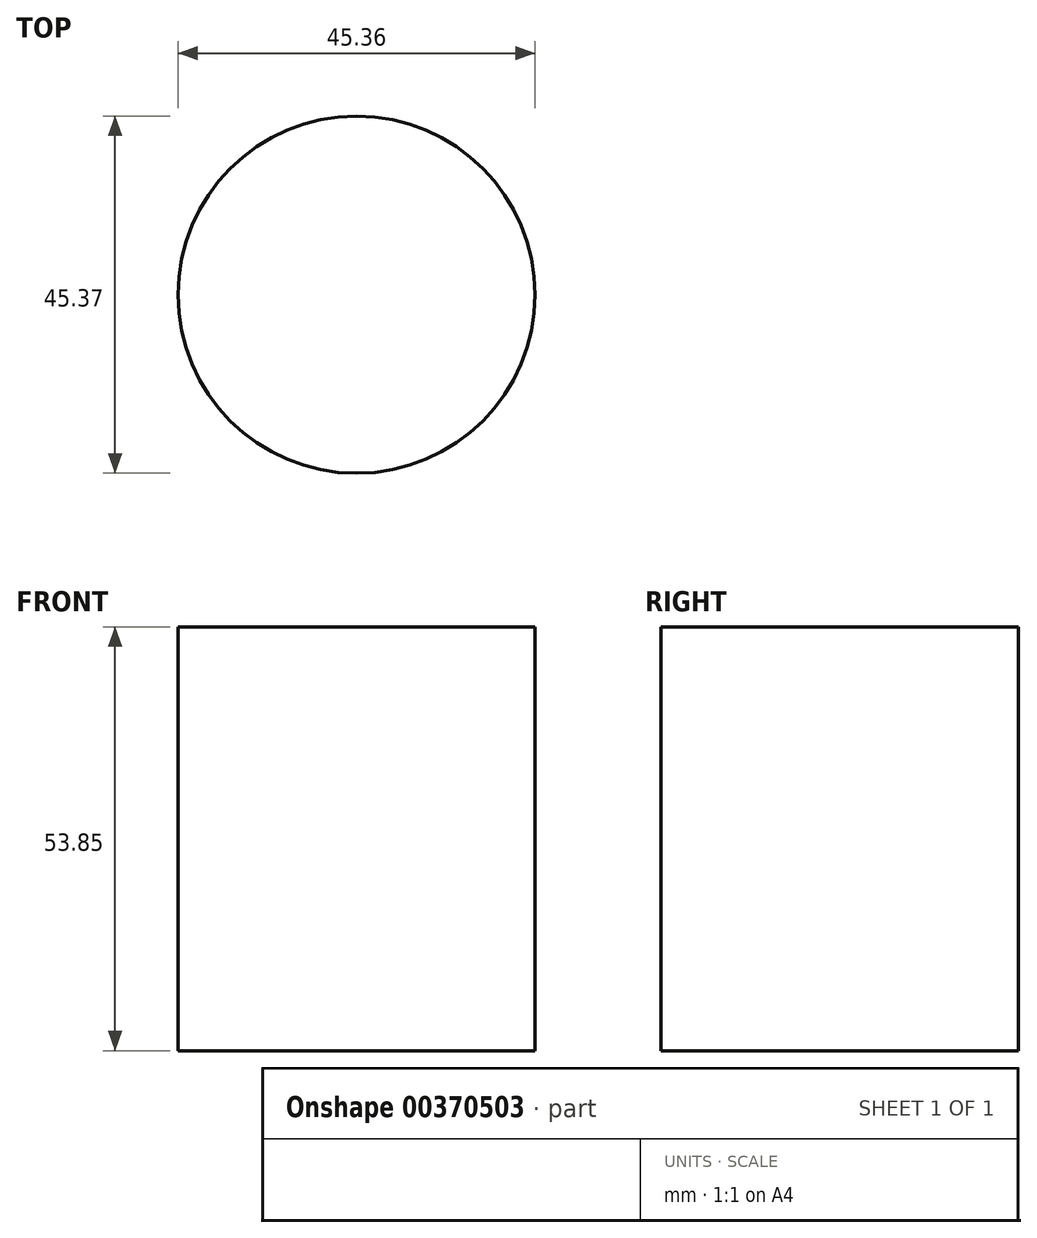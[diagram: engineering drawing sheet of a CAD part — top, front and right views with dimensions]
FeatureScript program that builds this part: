
annotation { "Feature Type Name" : "Feature", "Feature Type Description" : "" }
export const myFeature = defineFeature(function(context is Context, id is Id, definition is map)
    precondition{}
    {
        {
            var Q0;
            Q0=qCreatedBy(makeId("Top.planeOp"),FACE);
            var sketch = newSketch(context, id + "F0", { "sketchPlane" : qUnion([Q0])});
            skCircle(sketch, "E0", {"center": v(26.86, -34.22) * mm, "radius": 22.68 * mm});
            skSolve(sketch);
        }
        {
            var Q0;
            Q0=makeQuery(id+"F0.imprint","IMPRINT",FACE,{"disambiguationData":[TD([[makeQuery(id+"F0.imprint","IMPRINT",EDGE,{"derivedFrom":sQuery(id+"F0.wireOp",EDGE,"E0")}),1.0]])]});
            extrude(context, id + "F1", {"entities" : qUnion([Q0]), "depth" : 53.85 * mm});
        }
    });
